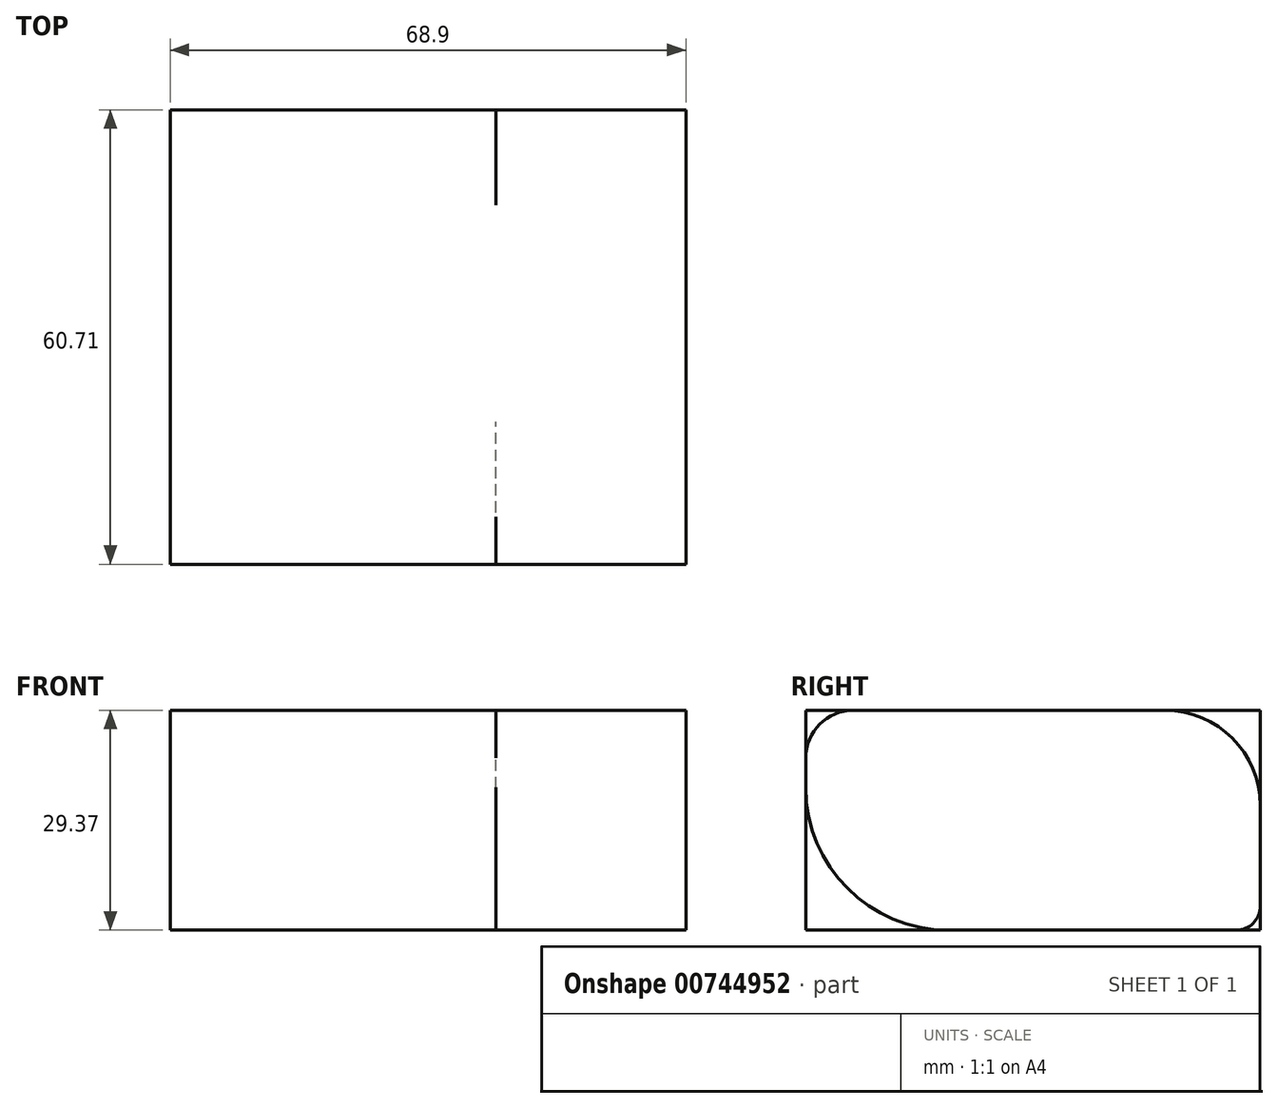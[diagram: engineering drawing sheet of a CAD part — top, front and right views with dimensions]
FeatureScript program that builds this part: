
annotation { "Feature Type Name" : "Feature", "Feature Type Description" : "" }
export const myFeature = defineFeature(function(context is Context, id is Id, definition is map)
    precondition{}
    {
        {
            var Q0;
            Q0=qCreatedBy(makeId("Front.planeOp"),FACE);
            var sketch = newSketch(context, id + "F0", { "sketchPlane" : qUnion([Q0])});
            skLineSegment(sketch, "E0.bottom", {"start": v(0, 0) * mm, "end": v(43.5, 0) * mm});
            skLineSegment(sketch, "E0.top", {"start": v(0, -29.37) * mm, "end": v(43.5, -29.37) * mm});
            skLineSegment(sketch, "E0.left", {"start": v(0, 0) * mm, "end": v(0, -29.37) * mm});
            skLineSegment(sketch, "E0.right", {"start": v(43.5, 0) * mm, "end": v(43.5, -29.37) * mm});
            skSolve(sketch);
        }
        {
            var Q0;
            Q0 = qSketchRegion(id + "F0", true);
            extrude(context, id + "F1", {"entities" : qUnion([Q0]), "depth" : 60.7 * mm, "offsetDistance" : 25.4 * mm});
        }
        {
            var Q0;
            Q0=makeQuery(id+"F1.opExtrude","SWEPT_FACE",FACE,{"disambiguationData":[OSD([sQuery(id+"F0.wireOp",EDGE,"E0.right")])]});
            var sketch = newSketch(context, id + "F2", { "sketchPlane" : qUnion([Q0])});
            skLineSegment(sketch, "E1.0.0", {"start": v(0, -26.2) * mm, "end": v(0, -12.7) * mm});
            skLineSegment(sketch, "E1.0.1", {"start": v(-12.7, 0) * mm, "end": v(-54.36, 0) * mm});
            skLineSegment(sketch, "E1.0.2", {"start": v(-60.7, -6.35) * mm, "end": v(-60.7, -10.32) * mm});
            skLineSegment(sketch, "E1.0.3", {"start": v(-41.66, -29.37) * mm, "end": v(-3.17, -29.37) * mm});
            skPoint(sketch, "E2.visualSharp", {"position": v(-60.7, 0) * mm});
            skArc(sketch, "E2.filletArc", {"start": v(-54.36, 0) * mm, "mid": v(-58.85, -1.86) * mm, "end": v(-60.7, -6.35) * mm});
            skPoint(sketch, "E3.visualSharp", {"position": v(0, 0) * mm});
            skArc(sketch, "E3.filletArc", {"start": v(0, -12.7) * mm, "mid": v(-3.72, -3.72) * mm, "end": v(-12.7, 0) * mm});
            skPoint(sketch, "E4.visualSharp", {"position": v(-60.7, -29.37) * mm});
            skArc(sketch, "E4.filletArc", {"start": v(-60.7, -10.32) * mm, "mid": v(-55.13, -23.79) * mm, "end": v(-41.66, -29.37) * mm});
            skPoint(sketch, "E5.visualSharp", {"position": v(0, -29.37) * mm});
            skArc(sketch, "E5.filletArc", {"start": v(-3.17, -29.37) * mm, "mid": v(-0.93, -28.44) * mm, "end": v(0, -26.2) * mm});
            skSolve(sketch);
        }
        {
            var Q0;
            Q0 = qSketchRegion(id + "F2", true);
            extrude(context, id + "F3", {"entities" : qUnion([Q0]), "operationType" : NewBodyOperationType.ADD, "depth" : 25.4 * mm, "offsetDistance" : 25.4 * mm});
        }
    });
